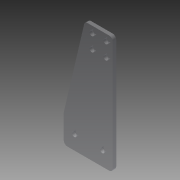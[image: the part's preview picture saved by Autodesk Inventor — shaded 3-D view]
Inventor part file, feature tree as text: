
AUTODESK INVENTOR PART (.ipt)
format: ipt  version: 2014 (Build 180170000, 170)  size: 174,592 bytes
history: native  units: in
note: dims shown in document units (in); Inventor stores cm internally (conversion verified against a paired STEP export)
features: other x3, sheet_metal_op x1, fillet x1, sketch x1
ambient origin geometry x8: Origin, YZ Plane, XZ Plane, XY Plane, X Axis, Y Axis, Z Axis, Center Point
bodies: Solid1 (feature_tree)
feature tree (6):
  sheet_metal_op  "Face1"
  fillet  "Fillet5"  Radius=4.1875in
  sketch  "Sketch1"  dims[d2=0.163in d4=0.7874in d6=1.0in d7=0.3937in d9=1.0in d11=0.125in d22=0.5in d50=1.0in d51=1.75in d52=1.0in d53=0.375in d56=0.163in d57=0.25in d58=0.25in d59=0.7874in d61=0.5in d62=0.7874in d64=0.5in d67=0.125in d3=0.125in]
  other  "Plate1"
  other  "Definition1"
  other  "Cut1"
